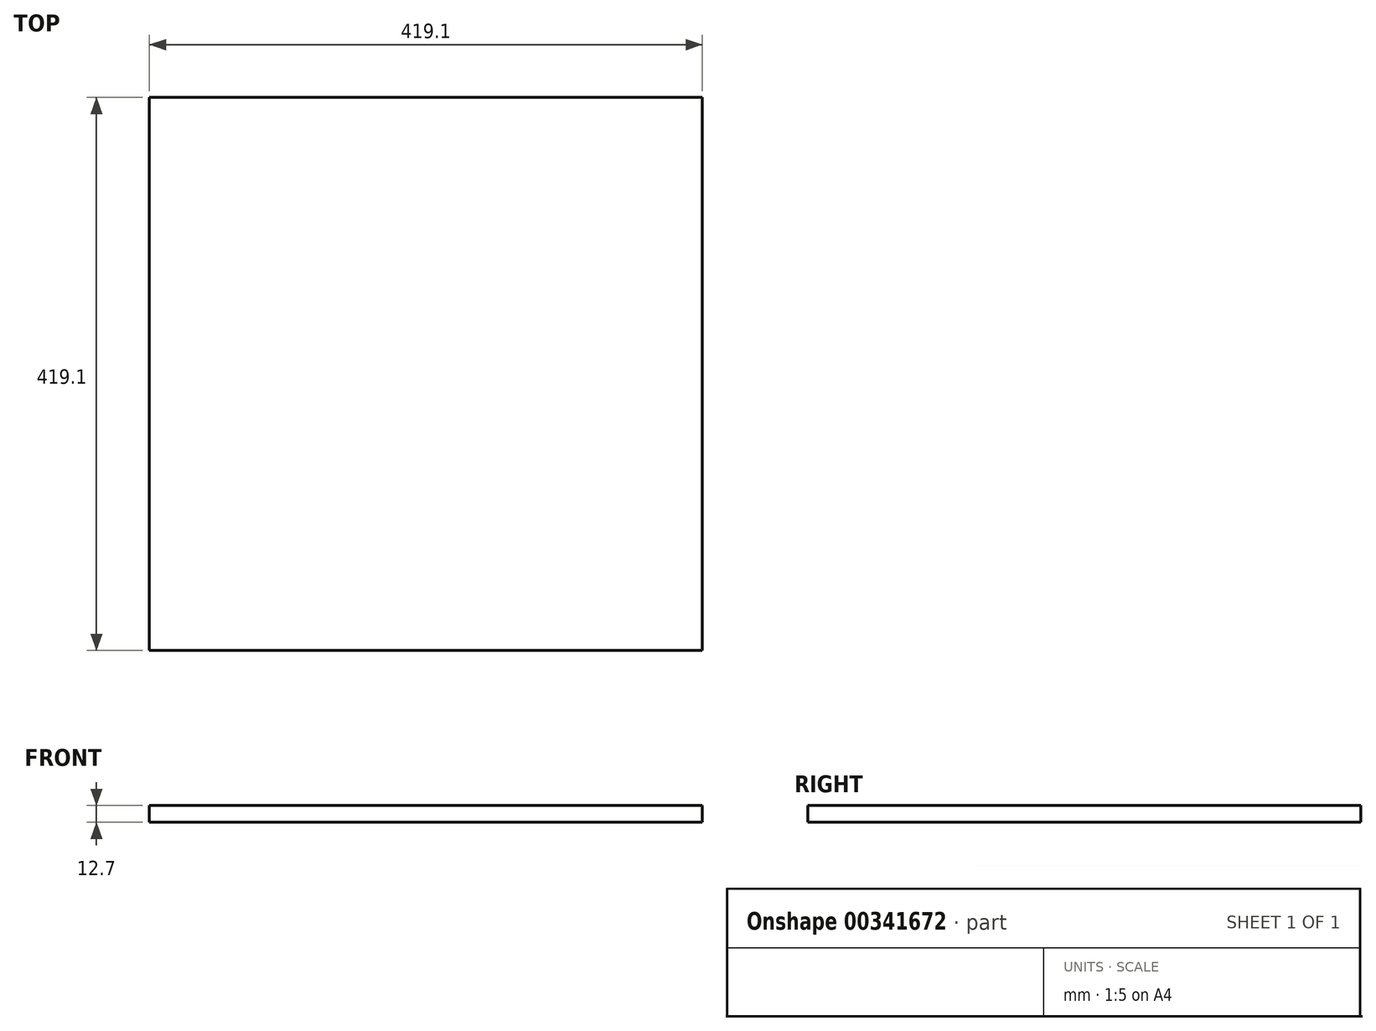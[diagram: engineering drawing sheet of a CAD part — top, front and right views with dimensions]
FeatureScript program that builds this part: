
annotation { "Feature Type Name" : "Feature", "Feature Type Description" : "" }
export const myFeature = defineFeature(function(context is Context, id is Id, definition is map)
    precondition{}
    {
        {
            var Q0;
            Q0=qCreatedBy(makeId("Top.planeOp"),FACE);
            var sketch = newSketch(context, id + "F0", { "sketchPlane" : qUnion([Q0])});
            skLineSegment(sketch, "E0.bottom", {"start": v(-200.48, 267.95) * mm, "end": v(218.62, 267.95) * mm});
            skLineSegment(sketch, "E0.top", {"start": v(-200.48, -151.15) * mm, "end": v(218.62, -151.15) * mm});
            skLineSegment(sketch, "E0.left", {"start": v(-200.48, 267.95) * mm, "end": v(-200.48, -151.15) * mm});
            skLineSegment(sketch, "E0.right", {"start": v(218.62, 267.95) * mm, "end": v(218.62, -151.15) * mm});
            skSolve(sketch);
        }
        {
            var Q0;
            Q0=makeQuery(id+"F0.imprint","IMPRINT",FACE,{"disambiguationData":[TD([[makeQuery(id+"F0.imprint","IMPRINT",EDGE,{"derivedFrom":sQuery(id+"F0.wireOp",EDGE,"E0.bottom")}),-1.0]])]});
            extrude(context, id + "F1", {"entities" : qUnion([Q0]), "depth" : 12.7 * mm, "offsetDistance" : 25.4 * mm});
        }
    });
